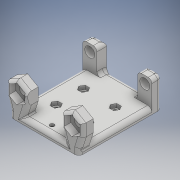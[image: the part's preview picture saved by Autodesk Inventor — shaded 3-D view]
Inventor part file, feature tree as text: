
AUTODESK INVENTOR PART (.ipt)
format: ipt  version: 2018 (Build 220112000, 112)  size: 469,504 bytes
history: native  units: mm
features: sketch x9, extrude x8, fillet x3, other x3, reference x2
ambient origin geometry x8: Origin, YZ Plane, XZ Plane, XY Plane, X Axis, Y Axis, Z Axis, Center Point
bodies: Solid1 (feature_tree)
feature tree (25):
  extrude  "Extrusion1"  Depth=56.8mm
  extrude  "Extrusion2"  Depth=6.5mm
  extrude  "Extrusion3"  Depth=3.0mm
  extrude  "Extrusion4"  Depth=8.2mm
  extrude  "Extrusion5"  Depth=20.0mm
  extrude  "Extrusion6"  Depth=13.3mm
  fillet  "Fillet2"  Radius=2.0mm
  fillet  "Fillet3"  Radius=6.0mm
  fillet  "Fillet4"  Radius=8.1mm
  sketch  "Sketch7"  dims[d21=3.0mm d22=0.0mm d23=3.4mm]
  extrude  "Extrusion7"  Depth=3.4mm
  extrude  "Extrusion8"  Depth=1.0mm
  sketch  "Sketch1"  dims[d0=67.984mm d1=56.8mm]
  sketch  "Sketch2"  dims[d2=5.0mm d3=0.0mm d5=6.5mm]
  reference  "Reference1"
  reference  "Reference2"
  sketch  "Sketch3"  dims[d6=3.0mm d7=0.0mm d8=3.5mm]
  sketch  "Sketch4"  dims[d9=0.0mm d10=0.0mm d11=8.2mm]
  sketch  "Sketch5"  dims[d12=6.0mm d13=20.0mm]
  sketch  "Sketch6"  dims[d14=8.0mm d15=0.0mm d16=13.3mm d17=2.0mm d18=6.0mm d19=0.0mm d20=8.1mm]
  sketch  "Sketch8"  dims[d24=3.0mm d25=1.0mm]
  sketch  "Sketch9"  dims[d26=3.0mm d27=3.5mm d28=10.0mm d29=0.0mm d30=6.0mm d31=3.0mm d32=0.0mm]
  parser-record x1  (decoder bookkeeping rows leaked as tree rows — omitted from the tree; the rows remain in map.json)
  other  "Plotter.iam"
  other  "x-carriage-with-endstop-trigger:1"
note: 1 file-system path scrubbed to <path> (originals preserved in map.json)
